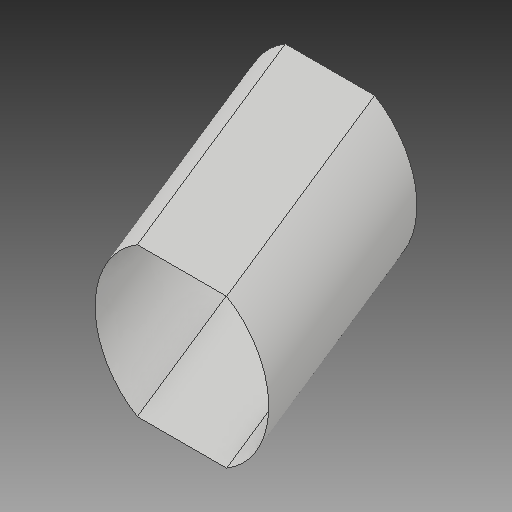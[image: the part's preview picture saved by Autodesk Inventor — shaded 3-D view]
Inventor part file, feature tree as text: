
AUTODESK INVENTOR PART (.ipt)
format: ipt  version: 2017 (Build 210142000, 142)  size: 113,664 bytes
history: native  units: in
note: dims shown in document units (in); Inventor stores cm internally (conversion verified against a paired STEP export)
features: sketch x2, plane x1, sweep x1, delete_face x1
ambient origin geometry x8: Origin, YZ Plane, XZ Plane, XY Plane, X Axis, Y Axis, Z Axis, Center Point
bodies: Solid1 (feature_tree)
feature tree (5):
  sketch  "Sketch1"  dims[d28=8.0in d30=0.0in d31=0.0in]
  plane  "Work Plane2"
  sweep  "ramp"
  delete_face  "Delete Face1"
  sketch  "Sketch6"  dims[d59=3.3333in d61=3.3333in d62=0.8521in d63=4.0in d65=3.8873in d66=3.8873in d70=1.6458in d76=3.3333in]
